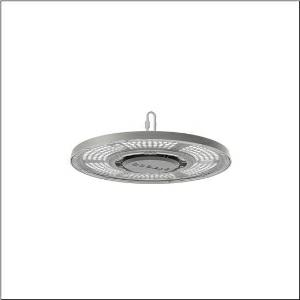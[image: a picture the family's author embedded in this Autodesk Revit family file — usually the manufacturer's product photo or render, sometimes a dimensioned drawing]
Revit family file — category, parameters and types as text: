
# Revit family: highbay_31-s_51hc427a4jmb
name_source: partatom
category: Lighting Fixtures
units: mm (PartAtom-declared; Revit-internal decimal feet)

## family parameters
Cut with Voids When Loaded = No
Host = Face
Light Source = No
Part Type = Normal
Room Calculation Point = No
Round Connector Dimension = Use Diameter
Shared = No

## types (1)
- Highbay 31-S (1 x LED, 20000 lm, 134 W, 4000K)
    Apparent Load = 134 VA
    CIE Flux Codes = 77 99 100 100 100
    Color Rendering = 80
    Color Temperature = 4000K
    Default Elevation = 1800 mm
    Description = Highbay 31-S, LED high bay luminaire, primary light control with lens, of PC, primary optical cover: cover panel, of PC, transparent, light emission: direct distribution, primary light characteristic: rotationally symmetric, installation type: suspended mounting, surface-mounted, LED, rated luminous flux: 20.000lm, luminous efficacy: 150lm/W, light colour: 840, colour temperature: 4000K, control gear: ECG, with cable, 3x 1.0mm², free wire ends, mains connection: 220..240V, AC/DC, 0/50..60Hz, cable length: 1,5m, rated input power: 134W, housing, rotationally symmetric, of diecast aluminium, grey aluminium (RAL 9007), diameter: 339mm, protection rating (complete): IP65, insulation class (complete): insulation class I (protective earthing), certification: CE, ENEC, UKCA, protection symbol: D, impact resistance: IK08, permissible operating ambient temperature: -30..+45°C, standard: EN 60598-2-22, EN 60598, corresponds to IFS (International Featured Standards) requirements for safety and quality in the food industry, packaging unit: 1 piece
    Height = 141 mm
    Lamp = 1 x LED
    Lamp Light Flux = 20000 lm
    Lamp Power = 134 W
    Lamp count = 1
    Length = 339 mm
    Luminous efficacy = 149 lm/W
    Manufacturer = Siteco
    ModVariant = No
    Model = 51HC427A4JMB
    Mounting Place = Ceiling
    Mounting Type = Pendant
    Number of Poles = 1
    OnlyDefault = Yes
    Power Factor = 1
    Product Name = Highbay 31-S
    Product group = LED high bay luminaire
    ProductGroupID = 903
    Protection Class = Protection class I
    Protection Degree = IP 65
    RLX_Detail_Level = 1
    RlxData = <blob elided: 163061 chars, md5=58a24571>
    Socket = socket
    Standby Power = 0 W
    System Light Flux = 20000 lm
    System Power = 134 W
    Type Comments = Product without accessories
    Type Image = l_1007237.jpg
    URL = http://relux.com
    VarID = ---
    Voltage = 0 V
    Weight = 0.00 kg
    Width = 0 mm  [stored 0 ft]

note: [stored X ft] marks values corroborated as IEEE doubles in the binary element streams (Revit-internal decimal feet)

## geometry (parser evidence)
native form markers: Blend x4, Sweep x10
no freeform markers — native parametric forms only
